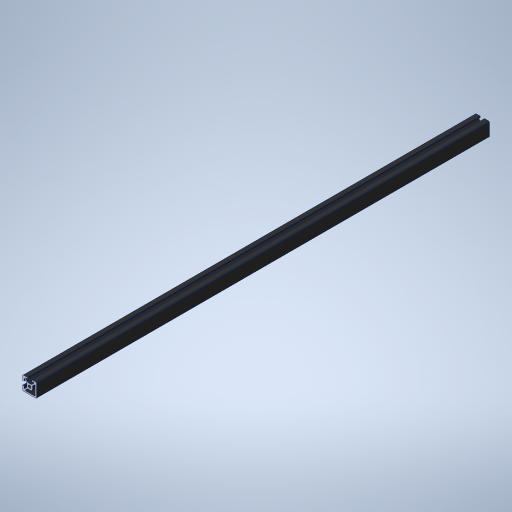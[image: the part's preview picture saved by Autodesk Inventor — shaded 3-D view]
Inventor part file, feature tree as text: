
AUTODESK INVENTOR PART (.ipt)
format: ipt  version: 2024 (Build 280153000, 153)  size: 361,984 bytes
history: native  units: mm
features: other x7, thread x2, sketch x2, extrude x1, hole x1
ambient origin geometry x8: Origin, YZ Plane, XZ Plane, XY Plane, X Axis, Y Axis, Z Axis, Center Point
bodies: Solid1 (feature_tree)
feature tree (13):
  extrude  "Extrusion1"  TaperAngle=0.0deg  [1 undecoded]
  hole  "Hole1"  [1 undecoded]
  other  "C1_XY"
  other  "C1_YZ"
  other  "C1_ZX"
  other  "C1_X"
  other  "C1_Y"
  other  "C1_Z"
  other  "C1_Center"
  thread  "Thread1"  [1 undecoded]
  thread  "Thread2"  [1 undecoded]
  sketch  "Sketch_64"  dims[d2=4.2mm d3=6.0mm d4=4.0mm d5=2.0mm d6=90.0deg d7=680.0mm d8=0.0mm d9=0.0mm d10=10.0mm d11=0.0mm d12=10.0mm d13=0.0mm]
  sketch  "Sketch2"  dims[d0=650.0mm d1=0.0mm]
note: 4 required parameter values undecoded (feature->parameter linkage not recoverable at this tier; creation-order binding heuristic only, values carry confidence <= 0.55)
